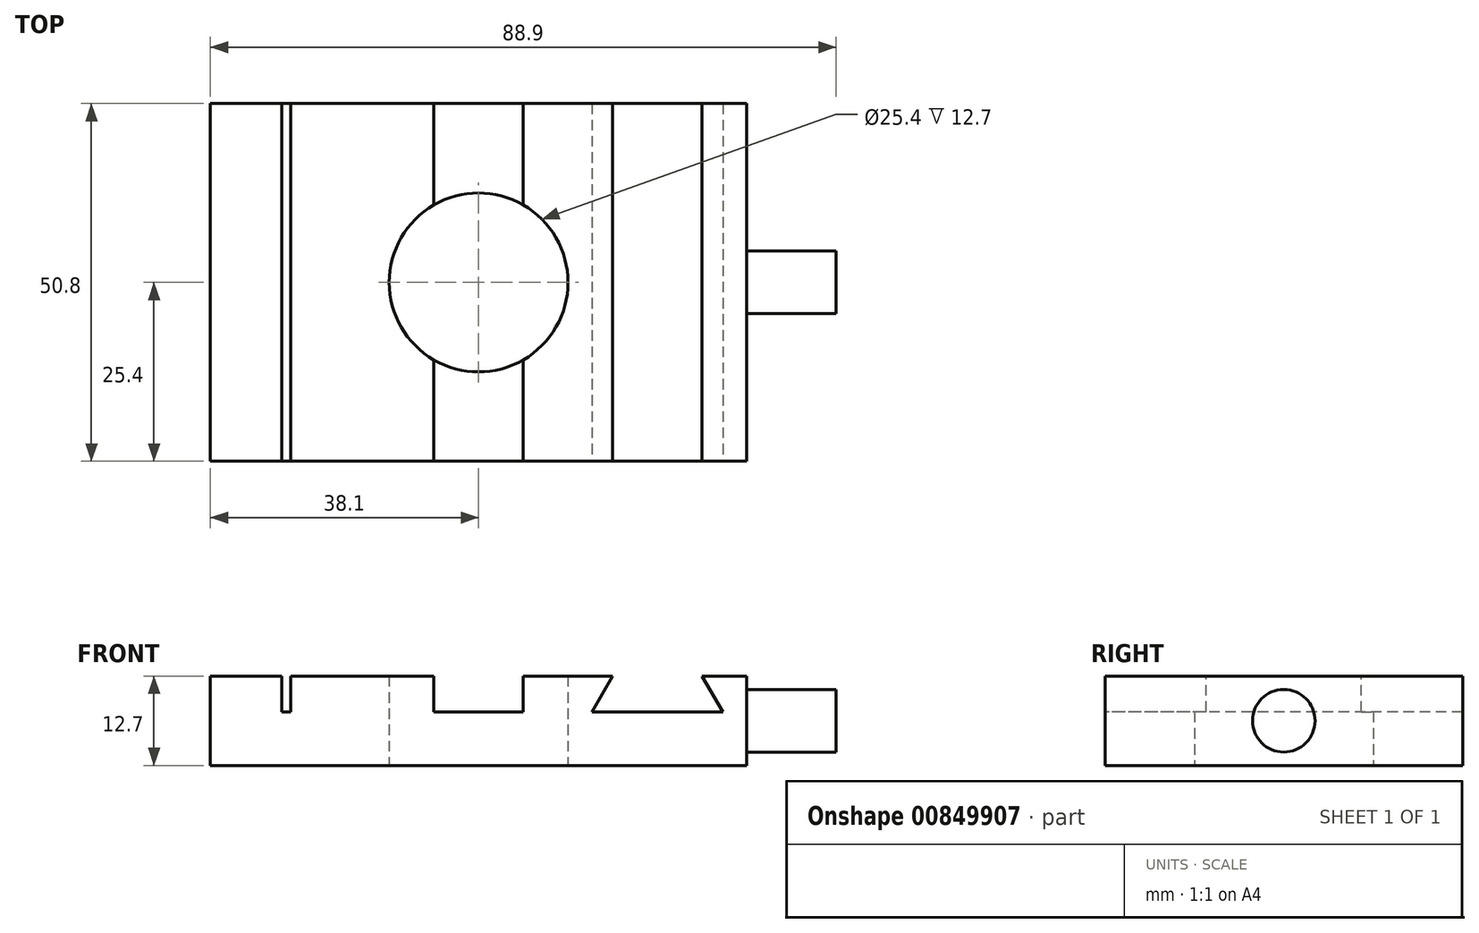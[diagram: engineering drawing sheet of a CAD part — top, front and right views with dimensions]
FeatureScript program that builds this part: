
annotation { "Feature Type Name" : "Feature", "Feature Type Description" : "" }
export const myFeature = defineFeature(function(context is Context, id is Id, definition is map)
    precondition{}
    {
        {
            var Q0;
            Q0=qCreatedBy(makeId("Top.planeOp"),FACE);
            var sketch = newSketch(context, id + "F0", { "sketchPlane" : qUnion([Q0])});
            skLineSegment(sketch, "E0.bottom", {"start": v(38.1, -25.4) * mm, "end": v(-38.1, -25.4) * mm});
            skLineSegment(sketch, "E0.top", {"start": v(38.1, 25.4) * mm, "end": v(-38.1, 25.4) * mm});
            skLineSegment(sketch, "E0.left", {"start": v(38.1, -25.4) * mm, "end": v(38.1, 25.4) * mm});
            skLineSegment(sketch, "E0.right", {"start": v(-38.1, -25.4) * mm, "end": v(-38.1, 25.4) * mm});
            skPoint(sketch, "E0.middle", {"position": v(0, 0) * mm});
            skCircle(sketch, "E1", {"center": v(0, 0) * mm, "radius": 12.7 * mm});
            skSolve(sketch);
        }
        {
            var Q0;
            Q0=makeQuery(id+"F0.imprint","IMPRINT",FACE,{"disambiguationData":[TD([[makeQuery(id+"F0.imprint","IMPRINT",EDGE,{"derivedFrom":sQuery(id+"F0.wireOp",EDGE,"E0.bottom")}),-1.0]])]});
            extrude(context, id + "F1", {"entities" : qUnion([Q0]), "depth" : 12.7 * mm, "offsetDistance" : 25.4 * mm});
        }
        {
            var Q0;
            Q0=makeQuery(id+"F1.opExtrude","CAP_FACE",FACE,{"disambiguationData":[OSD([sQuery(id+"F0.wireOp",EDGE,"E0.bottom"),sQuery(id+"F0.wireOp",EDGE,"E0.top"),sQuery(id+"F0.wireOp",EDGE,"E0.left"),sQuery(id+"F0.wireOp",EDGE,"E0.right"),sQuery(id+"F0.wireOp",EDGE,"E1")])],"isStart":false});
            var sketch = newSketch(context, id + "F2", { "sketchPlane" : qUnion([Q0])});
            skLineSegment(sketch, "E2.bottom", {"start": v(-27.94, 25.4) * mm, "end": v(-26.67, 25.4) * mm});
            skLineSegment(sketch, "E2.top", {"start": v(-27.94, -25.4) * mm, "end": v(-26.67, -25.4) * mm});
            skLineSegment(sketch, "E2.left", {"start": v(-27.94, 25.4) * mm, "end": v(-27.94, -25.4) * mm});
            skLineSegment(sketch, "E2.right", {"start": v(-26.67, 25.4) * mm, "end": v(-26.67, -25.4) * mm});
            skPoint(sketch, "E3", {"position": v(0, 0) * mm});
            skLineSegment(sketch, "E4.bottom", {"start": v(-6.35, 25.4) * mm, "end": v(6.35, 25.4) * mm});
            skLineSegment(sketch, "E4.top", {"start": v(-6.35, -25.4) * mm, "end": v(6.35, -25.4) * mm});
            skLineSegment(sketch, "E4.left", {"start": v(-6.35, 25.4) * mm, "end": v(-6.35, -25.4) * mm});
            skLineSegment(sketch, "E4.right", {"start": v(6.35, 25.4) * mm, "end": v(6.35, -25.4) * mm});
            skLineSegment(sketch, "E5", {"start": v(0, 25.4) * mm, "end": v(0, -25.4) * mm, "construction": true});
            skSolve(sketch);
        }
        {
            var Q0;
            Q0=makeQuery(id+"F2.imprint","IMPRINT",FACE,{"disambiguationData":[TD([[makeQuery(id+"F2.imprint","IMPRINT",EDGE,{"derivedFrom":sQuery(id+"F2.wireOp",EDGE,"E2.bottom")}),1.0]])]});
            var Q1;
            {var subQ0=sQuery(id+"F2.wireOp",EDGE,"E4.top");Q1=makeQuery(id+"F2.imprint","IMPRINT",FACE,{"disambiguationData":[TD([[makeQuery(id+"F2.imprint","IMPRINT",EDGE,{"derivedFrom":subQ0}),-1.0]])]});}
            var Q2;
            {var subQ0=sQuery(id+"F2.wireOp",EDGE,"E4.bottom");Q2=makeQuery(id+"F2.imprint","IMPRINT",FACE,{"disambiguationData":[TD([[makeQuery(id+"F2.imprint","IMPRINT",EDGE,{"derivedFrom":subQ0}),1.0]])]});}
            extrude(context, id + "F3", {"entities" : qUnion([Q0, Q1, Q2]), "operationType" : NewBodyOperationType.REMOVE, "oppositeDirection" : true, "depth" : 5.08 * mm, "offsetDistance" : 25.4 * mm});
        }
        {
            var Q0;
            Q0=makeQuery(id+"F1.opExtrude","SWEPT_FACE",FACE,{"disambiguationData":[OSD([sQuery(id+"F0.wireOp",EDGE,"E0.bottom")])]});
            var sketch = newSketch(context, id + "F4", { "sketchPlane" : qUnion([Q0])});
            skLineSegment(sketch, "E6", {"start": v(19.05, 12.7) * mm, "end": v(16.12, 7.62) * mm});
            skLineSegment(sketch, "E7", {"start": v(16.12, 7.62) * mm, "end": v(34.68, 7.62) * mm});
            skLineSegment(sketch, "E8", {"start": v(34.68, 7.62) * mm, "end": v(31.75, 12.7) * mm});
            skLineSegment(sketch, "E9", {"start": v(31.75, 12.7) * mm, "end": v(19.05, 12.7) * mm});
            skLineSegment(sketch, "E10", {"start": v(25.4, 7.62) * mm, "end": v(25.4, 12.7) * mm, "construction": true});
            skSolve(sketch);
        }
        {
            var Q0;
            Q0=makeQuery(id+"F4.imprint","IMPRINT",FACE,{"disambiguationData":[TD([[makeQuery(id+"F4.imprint","IMPRINT",EDGE,{"derivedFrom":sQuery(id+"F4.wireOp",EDGE,"E6")}),1.0]])]});
            extrude(context, id + "F5", {"entities" : qUnion([Q0]), "operationType" : NewBodyOperationType.REMOVE, "endBound" : BoundingType.THROUGH_ALL, "oppositeDirection" : true, "depth" : 25.4 * mm, "offsetDistance" : 25.4 * mm});
        }
        {
            var Q0;
            Q0=makeQuery(id+"F1.opExtrude","SWEPT_FACE",FACE,{"disambiguationData":[OSD([sQuery(id+"F0.wireOp",EDGE,"E0.left")])]});
            var sketch = newSketch(context, id + "F6", { "sketchPlane" : qUnion([Q0])});
            skCircle(sketch, "E11", {"center": v(0, 6.35) * mm, "radius": 4.45 * mm});
            skPoint(sketch, "E11.centerSnap0", {"position": v(-25.4, 6.35) * mm});
            skPoint(sketch, "E11.centerSnap1", {"position": v(0, 12.7) * mm});
            skSolve(sketch);
        }
        {
            var Q0;
            Q0=makeQuery(id+"F6.imprint","IMPRINT",FACE,{"disambiguationData":[TD([[makeQuery(id+"F6.imprint","IMPRINT",EDGE,{"derivedFrom":sQuery(id+"F6.wireOp",EDGE,"E11")}),1.0]])]});
            extrude(context, id + "F7", {"entities" : qUnion([Q0]), "operationType" : NewBodyOperationType.ADD, "depth" : 12.7 * mm, "offsetDistance" : 25.4 * mm});
        }
    });
